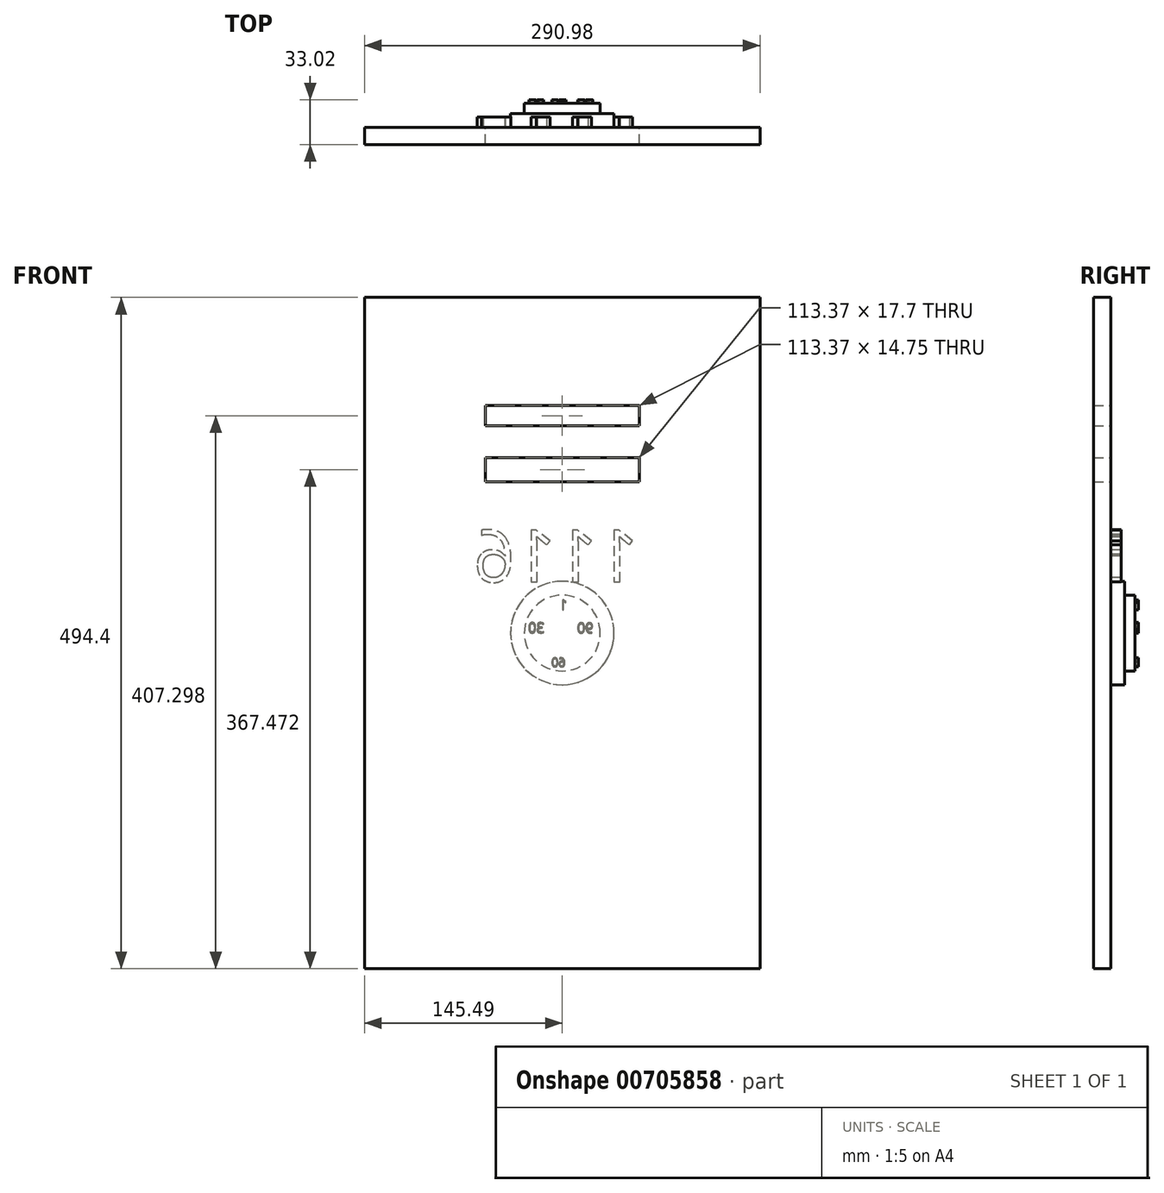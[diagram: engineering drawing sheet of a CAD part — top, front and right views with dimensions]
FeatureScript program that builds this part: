
annotation { "Feature Type Name" : "Feature", "Feature Type Description" : "" }
export const myFeature = defineFeature(function(context is Context, id is Id, definition is map)
    precondition{}
    {
        {
            var Q0;
            Q0=qCreatedBy(makeId("Front.planeOp"),FACE);
            var sketch = newSketch(context, id + "F0", { "sketchPlane" : qUnion([Q0])});
            skLineSegment(sketch, "E0.bottom", {"start": v(-145.49, -247.2) * mm, "end": v(145.49, -247.2) * mm});
            skLineSegment(sketch, "E0.top", {"start": v(-145.49, 247.2) * mm, "end": v(145.49, 247.2) * mm});
            skLineSegment(sketch, "E0.left", {"start": v(-145.49, -247.2) * mm, "end": v(-145.49, 247.2) * mm});
            skLineSegment(sketch, "E0.right", {"start": v(145.49, -247.2) * mm, "end": v(145.49, 247.2) * mm});
            skPoint(sketch, "E0.middle", {"position": v(0, 0) * mm});
            skLineSegment(sketch, "E1.bottom", {"start": v(-56.68, 167.47) * mm, "end": v(56.68, 167.47) * mm});
            skLineSegment(sketch, "E1.top", {"start": v(-56.68, 152.72) * mm, "end": v(56.68, 152.72) * mm});
            skLineSegment(sketch, "E1.left", {"start": v(-56.68, 167.47) * mm, "end": v(-56.68, 152.72) * mm});
            skLineSegment(sketch, "E1.right", {"start": v(56.68, 167.47) * mm, "end": v(56.68, 152.72) * mm});
            skPoint(sketch, "E1.middle", {"position": v(0, 160.1) * mm});
            skLineSegment(sketch, "E2.bottom", {"start": v(-56.68, 111.42) * mm, "end": v(56.68, 111.42) * mm});
            skLineSegment(sketch, "E2.top", {"start": v(-56.68, 129.12) * mm, "end": v(56.68, 129.12) * mm});
            skLineSegment(sketch, "E2.left", {"start": v(-56.68, 111.42) * mm, "end": v(-56.68, 129.12) * mm});
            skLineSegment(sketch, "E2.right", {"start": v(56.68, 111.42) * mm, "end": v(56.68, 129.12) * mm});
            skPoint(sketch, "E2.middle", {"position": v(0, 120.27) * mm});
            skPoint(sketch, "E2.middle.positionSnap0", {"position": v(0, 152.72) * mm});
            skPoint(sketch, "E2.centerSnap0", {"position": v(0, 152.72) * mm});
            skSolve(sketch);
        }
        {
            var Q0;
            Q0 = qSketchRegion(id + "F0", true);
            extrude(context, id + "F1", {"entities" : qUnion([Q0]), "depth" : 12.7 * mm, "offsetDistance" : 25.4 * mm});
        }
        {
            var Q0;
            Q0=makeQuery(id+"F1.opExtrude","CAP_FACE",FACE,{"disambiguationData":[OSD([sQuery(id+"F0.wireOp",EDGE,"E0.bottom"),sQuery(id+"F0.wireOp",EDGE,"E0.top"),sQuery(id+"F0.wireOp",EDGE,"E0.left"),sQuery(id+"F0.wireOp",EDGE,"E0.right"),sQuery(id+"F0.wireOp",EDGE,"E1.bottom"),sQuery(id+"F0.wireOp",EDGE,"E1.top"),sQuery(id+"F0.wireOp",EDGE,"E1.left"),sQuery(id+"F0.wireOp",EDGE,"E1.right"),sQuery(id+"F0.wireOp",EDGE,"E2.bottom"),sQuery(id+"F0.wireOp",EDGE,"E2.top"),sQuery(id+"F0.wireOp",EDGE,"E2.left"),sQuery(id+"F0.wireOp",EDGE,"E2.right")])],"isStart":true});
            var sketch = newSketch(context, id + "F2", { "sketchPlane" : qUnion([Q0])});
            skText(sketch, "E3", { "text": "1116", "fontName": "OpenSans-Regular.ttf"});
            const initialGuessF2  = {"E3": [-0.05668, 0.03767, 1, 0, 0.03835]};
            skSetInitialGuess(sketch, initialGuessF2);
            skSolve(sketch);
        }
        {
            var Q0;
            Q0 = qSketchRegion(id + "F2", true);
            extrude(context, id + "F3", {"entities" : qUnion([Q0]), "operationType" : NewBodyOperationType.ADD, "depth" : 7.62 * mm, "offsetDistance" : 25.4 * mm});
        }
        {
            var Q0;
            {var subQ0=sQuery(id+"F0.wireOp",EDGE,"E2.bottom");var subQ1=sQuery(id+"F0.wireOp",EDGE,"E1.right");var subQ2=sQuery(id+"F0.wireOp",EDGE,"E1.left");var subQ3=sQuery(id+"F0.wireOp",EDGE,"E1.top");var subQ4=sQuery(id+"F0.wireOp",EDGE,"E1.bottom");var subQ5=sQuery(id+"F0.wireOp",EDGE,"E2.top");var subQ6=sQuery(id+"F0.wireOp",EDGE,"E0.bottom");var subQ7=sQuery(id+"F0.wireOp",EDGE,"E0.right");var subQ8=sQuery(id+"F0.wireOp",EDGE,"E0.top");var subQ9=sQuery(id+"F0.wireOp",EDGE,"E0.left");var subQ10=sQuery(id+"F0.wireOp",EDGE,"E2.left");var subQ11=sQuery(id+"F0.wireOp",EDGE,"E2.right");Q0=makeQuery(id+"F3.boolean.opBoolean","SPLIT",FACE,{"disambiguationData":[TD([makeQuery(id+"F1.opExtrude","SWEPT_FACE",FACE,{"disambiguationData":[OSD([subQ6])]})])],"derivedFrom":makeQuery(id+"F1.opExtrude","CAP_FACE",FACE,{"disambiguationData":[OSD([subQ6,subQ8,subQ9,subQ7,subQ4,subQ3,subQ2,subQ1,subQ0,subQ5,subQ10,subQ11])],"isStart":true})});}
            var sketch = newSketch(context, id + "F4", { "sketchPlane" : qUnion([Q0])});
            skCircle(sketch, "E4", {"center": v(0, 0) * mm, "radius": 38.09 * mm});
            skSolve(sketch);
        }
        {
            var Q0;
            Q0 = qSketchRegion(id + "F4", true);
            extrude(context, id + "F5", {"entities" : qUnion([Q0]), "operationType" : NewBodyOperationType.ADD, "depth" : 10.16 * mm, "offsetDistance" : 25.4 * mm});
        }
        {
            var Q0;
            Q0=makeQuery(id+"F5.opExtrude","CAP_FACE",FACE,{"disambiguationData":[OSD([sQuery(id+"F4.wireOp",EDGE,"E4")])],"isStart":false});
            var sketch = newSketch(context, id + "F6", { "sketchPlane" : qUnion([Q0])});
            skCircle(sketch, "E5", {"center": v(0, 0) * mm, "radius": 27.92 * mm});
            skSolve(sketch);
        }
        {
            var Q0;
            Q0 = qSketchRegion(id + "F6", true);
            extrude(context, id + "F7", {"entities" : qUnion([Q0]), "operationType" : NewBodyOperationType.ADD, "depth" : 7.62 * mm, "offsetDistance" : 25.4 * mm});
        }
        {
            var Q0;
            Q0=makeQuery(id+"F7.opExtrude","CAP_FACE",FACE,{"disambiguationData":[OSD([sQuery(id+"F6.wireOp",EDGE,"E5")])],"isStart":false});
            var sketch = newSketch(context, id + "F8", { "sketchPlane" : qUnion([Q0])});
            skText(sketch, "E6", { "text": "1\n", "fontName": "OpenSans-Regular.ttf"});
            skText(sketch, "E7", { "text": "30", "fontName": "OpenSans-Regular.ttf"});
            skText(sketch, "E8", { "text": "60", "fontName": "OpenSans-Regular.ttf"});
            skText(sketch, "E9", { "text": "90", "fontName": "OpenSans-Regular.ttf"});
            const initialGuessF8  = {"E6": [-0.00384, 0.017, 1, 0, 0.00755], "E7": [0.01316, 0.00015, 1, 0, 0.00755], "E8": [-0.00238, -0.02486, 1, 0, 0.00657], "E9": [-0.02283, 0, 1, 0, 0.00751]};
            skSetInitialGuess(sketch, initialGuessF8);
            skSolve(sketch);
        }
        {
            var Q0;
            Q0 = qSketchRegion(id + "F8", true);
            extrude(context, id + "F9", {"entities" : qUnion([Q0]), "operationType" : NewBodyOperationType.ADD, "depth" : 2.54 * mm, "offsetDistance" : 25.4 * mm});
        }
    });
